# Revit family: WN-Frame Circular Arch-5x3-Assembly
name_source: partatom
category: Windows
units: mm (PartAtom-declared; Revit-internal decimal feet)

## family parameters
Always vertical = No
Cut with Voids When Loaded = No
Room Calculation Point = No
Shared = No
Work Plane-Based = Yes

## types (1)
- flex
    Default Elevation = 1.219 m
    Glass Thickness = 0.015 m
    Height = 3.596 m
    Height Constraint = 3.596 m
    Meeting Rail Y Offset = 0.02 m
    R1 = 0.878 m
    R2 = 0.828 m
    Width = 1.756 m
    Window Astragal Width = 0.015 m
    Window Bottom Sash Height = 1.394 m
    Window Bottom Sash Width = 1.656 m
    Window Frame Depth = 0.05 m
    Window Frame Material = <By Category>
    Window Frame Subsill Height = 0.06 m
    Window Frame Width = 0.05 m
    Window Glass Material = <By Category>
    Window Meeting Rail Height = 0.04 m
    Window Overall Frame Depth = 0.105 m
    Window Top Sash Height = 2.143 m
    Window Top Sash Width = 1.656 m
    X1 = 0.09 m
    X2 = 0.015 m

## geometry (parser evidence)
native form markers: Sweep x9
no freeform markers — native parametric forms only
